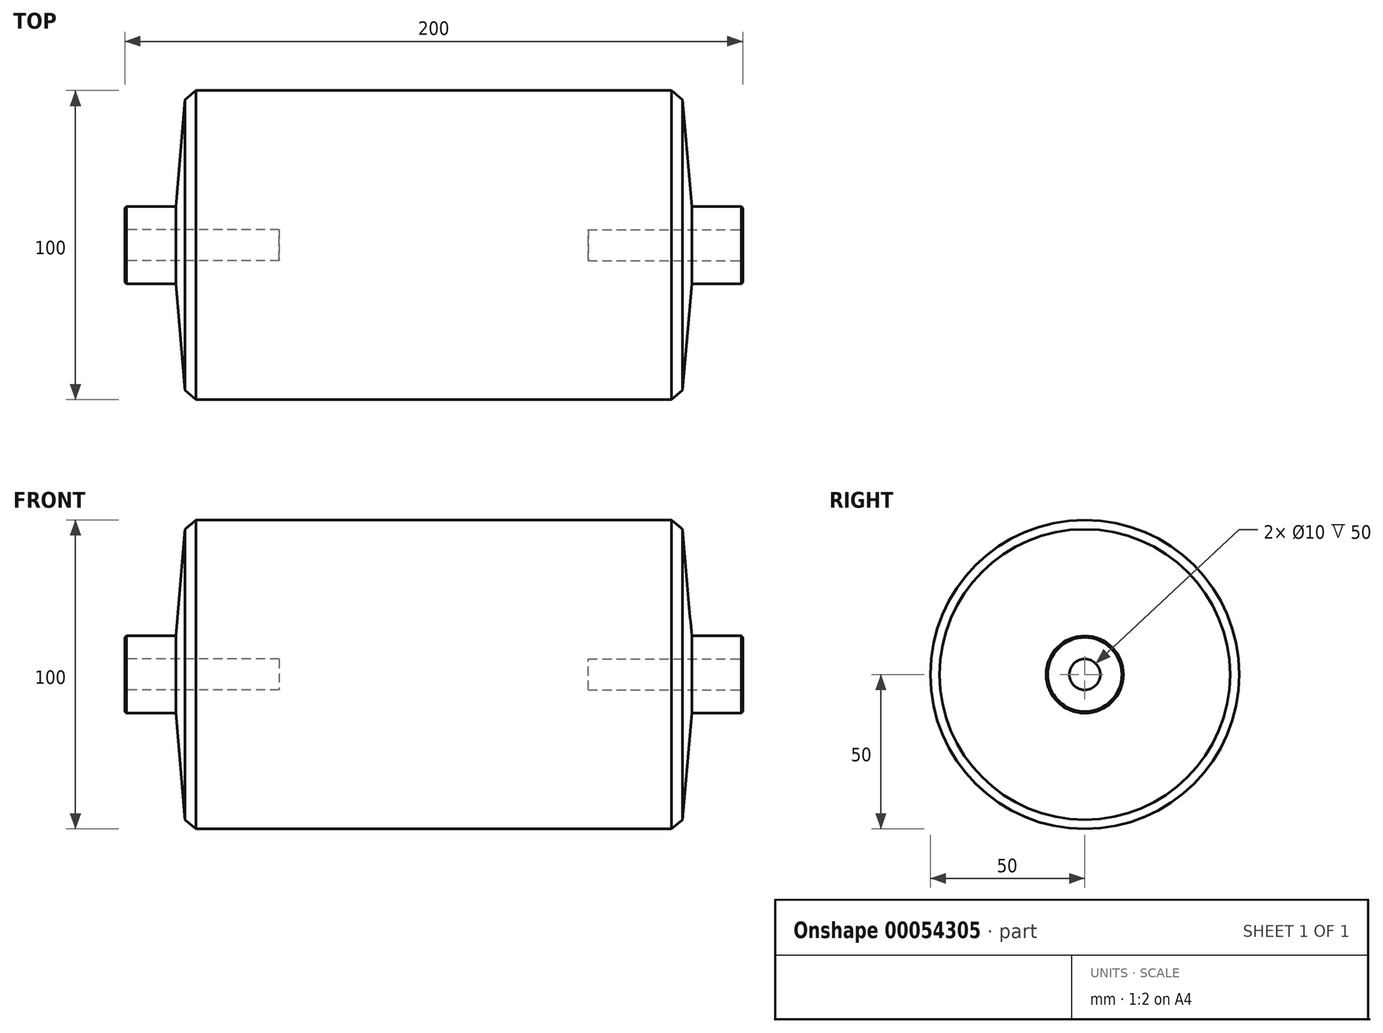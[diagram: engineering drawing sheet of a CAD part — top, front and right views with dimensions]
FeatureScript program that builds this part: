
annotation { "Feature Type Name" : "Feature", "Feature Type Description" : "" }
export const myFeature = defineFeature(function(context is Context, id is Id, definition is map)
    precondition{}
    {
        {
            var Q0;
            Q0=qCreatedBy(makeId("Top.planeOp"),FACE);
            var sketch = newSketch(context, id + "F0", { "sketchPlane" : qUnion([Q0])});
            skLineSegment(sketch, "E0", {"start": v(0, 0) * mm, "end": v(0, 12.5) * mm});
            skLineSegment(sketch, "E1", {"start": v(0, 12.5) * mm, "end": v(-16.5, 12.5) * mm});
            skLineSegment(sketch, "E2", {"start": v(-16.5, 12.5) * mm, "end": v(-19.8, 50) * mm});
            skLineSegment(sketch, "E3", {"start": v(-19.8, 50) * mm, "end": v(-180.23, 50) * mm});
            skLineSegment(sketch, "E4", {"start": v(-180.23, 50) * mm, "end": v(-183.5, 12.5) * mm});
            skLineSegment(sketch, "E5", {"start": v(-183.5, 12.5) * mm, "end": v(-200, 12.5) * mm});
            skLineSegment(sketch, "E6", {"start": v(-200, 12.5) * mm, "end": v(-200, 0) * mm});
            skLineSegment(sketch, "E7", {"start": v(-200, 0) * mm, "end": v(0, 0) * mm});
            skSolve(sketch);
        }
        {
            var Q0;
            Q0=makeQuery(id+"F0.imprint","IMPRINT",FACE,{"disambiguationData":[TD([[makeQuery(id+"F0.imprint","IMPRINT",EDGE,{"derivedFrom":sQuery(id+"F0.wireOp",EDGE,"E0")}),1.0]])]});
            var Q1;
            Q1=sQuery(id+"F0.wireOp",EDGE,"E7");
            revolve(context, id + "F1", {"entities" : qUnion([Q0]), "axis" : qUnion([Q1]), "revolveType" : RevolveType.FULL});
        }
        {
            var Q0;
            Q0=makeQuery(id+"F1.opRevolve","SWEPT_EDGE",EDGE,{"disambiguationData":[OSD([sQuery(id+"F0.wireOp",EDGE,"E3"),sQuery(id+"F0.wireOp",EDGE,"E4")])]});
            var Q1;
            Q1=makeQuery(id+"F1.opRevolve","SWEPT_EDGE",EDGE,{"disambiguationData":[OSD([sQuery(id+"F0.wireOp",EDGE,"E2"),sQuery(id+"F0.wireOp",EDGE,"E3")])]});
            chamfer(context, id + "F2", {"entities" : qUnion([Q0, Q1]), "chamferType" : ChamferType.OFFSET_ANGLE, "width" : 3 * mm, "oppositeDirection" : false, "angle" : 45 * degree, "tangentPropagation" : true});
        }
        {
            var Q0;
            Q0=makeQuery(id+"F1.opRevolve","SWEPT_EDGE",EDGE,{"disambiguationData":[OSD([sQuery(id+"F0.wireOp",EDGE,"E5"),sQuery(id+"F0.wireOp",EDGE,"E6")])]});
            var Q1;
            Q1=makeQuery(id+"F1.opRevolve","SWEPT_EDGE",EDGE,{"disambiguationData":[OSD([sQuery(id+"F0.wireOp",EDGE,"E0"),sQuery(id+"F0.wireOp",EDGE,"E1")])]});
            chamfer(context, id + "F3", {"entities" : qUnion([Q0, Q1]), "chamferType" : ChamferType.OFFSET_ANGLE, "width" : .5 * mm, "oppositeDirection" : false, "angle" : 45 * degree, "tangentPropagation" : true});
        }
        {
            var Q0;
            Q0=makeQuery(id+"F1.opRevolve","SWEPT_FACE",FACE,{"disambiguationData":[OSD([sQuery(id+"F0.wireOp",EDGE,"E0")])]});
            var sketch = newSketch(context, id + "F4", { "sketchPlane" : qUnion([Q0])});
            skCircle(sketch, "E8", {"center": v(0, 0) * mm, "radius": 5 * mm});
            skSolve(sketch);
        }
        {
            var Q0;
            Q0=makeQuery(id+"F4.imprint","IMPRINT",FACE,{"disambiguationData":[TD([[makeQuery(id+"F4.imprint","IMPRINT",EDGE,{"derivedFrom":sQuery(id+"F4.wireOp",EDGE,"E8")}),1.0]])]});
            var Q1;
            Q1=sQuery(id+"F4.wireOp",EDGE,"E8");
            extrude(context, id + "F5", {"entities" : qUnion([Q0]), "operationType" : NewBodyOperationType.REMOVE, "surfaceEntities" : qUnion([Q1]), "oppositeDirection" : true, "depth" : 50 * mm});
        }
        {
            var Q0;
            Q0=makeQuery(id+"F1.opRevolve","SWEPT_FACE",FACE,{"disambiguationData":[OSD([sQuery(id+"F0.wireOp",EDGE,"E6")])]});
            var sketch = newSketch(context, id + "F6", { "sketchPlane" : qUnion([Q0])});
            skCircle(sketch, "E9", {"center": v(0, 0) * mm, "radius": 5 * mm});
            skSolve(sketch);
        }
        {
            var Q0;
            Q0=makeQuery(id+"F6.imprint","IMPRINT",FACE,{"disambiguationData":[TD([[makeQuery(id+"F6.imprint","IMPRINT",EDGE,{"derivedFrom":sQuery(id+"F6.wireOp",EDGE,"E9")}),1.0]])]});
            var Q1;
            Q1=sQuery(id+"F6.wireOp",EDGE,"E9");
            extrude(context, id + "F7", {"entities" : qUnion([Q0]), "operationType" : NewBodyOperationType.REMOVE, "surfaceEntities" : qUnion([Q1]), "oppositeDirection" : true, "depth" : 50 * mm});
        }
    });
